# Revit family: Lighting_Fixture-Wall-Astro-Parma250
name_source: partatom
category: Lighting Fixtures
revit_build: Autodesk Revit 2014 (Build: 20130308_1515(x64)
units: mm (PartAtom-declared; Revit-internal decimal feet)

## types (1)
- 250
    Apparent Load = 9 VA
    Assembly Code = D5020200
    Cable Entry Placer (from right) = 54 mm  [stored 0.177165 ft]
    Cable Entry Placer (from top) = 25 mm  [stored 0.082021 ft]
    Casing Material = Astro - Plaster - Natural
    Class = 1
    Color Filter = 16777215
    Description = Wall light
    Diffuser From Wall = 4 mm  [stored 0.0131234 ft]
    Diffuser Width = 233 mm  [stored 0.764436 ft]
    Dimmable = No
    Dimming Lamp Color Temperature Shift = <None>
    Emit Shape Visible in Rendering = No
    Emit from Rectangle Length = 233 mm  [stored 0.764436 ft]
    Emit from Rectangle Width = 48 mm  [stored 0.15748 ft]
    Energy Efficiency Rating = -
    Heatsink Material = Astro - Aluminium - Anodised
    Height = 65 mm  [stored 0.213255 ft]
    IP Rating = IP20
    Lamp = LED
    Lamp included = Yes
    Length = 60 mm  [stored 0.19685 ft]
    Light Source Elevation = 1635 mm  [stored 5.36417 ft]
    Light Source From Wall = 30 mm  [stored 0.0984252 ft]
    Luminaire Lamp Efficiency Rating = -A
    Manufacturer = Astro Lighting Ltd, CM20 2DP
    Model = 0887 Parma 250
    Mountable on normally flammable surfaces = Yes
    Number of Poles = 1
    Photometric Web File = 0887 PARMA 250.ies
    Product Documentation = http://www.astrolighting.co.uk
    Suitable for bathroom zone = Zone 3
    Tilt Angle = -90.00°
    Type Comments = - Includes integral electronic driver
    URL = www.astrolighting.co.uk
    Voltage = 230 V
    Wattage Comments = 3X3W
    Weight = 0.9 kg
    Width = 250 mm  [stored 0.82021 ft]

note: [stored X ft] marks values corroborated as IEEE doubles in the binary element streams (Revit-internal decimal feet)

## geometry (parser evidence)
native form markers: Sweep x2
no freeform markers — native parametric forms only
